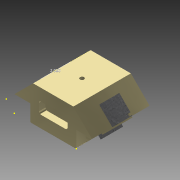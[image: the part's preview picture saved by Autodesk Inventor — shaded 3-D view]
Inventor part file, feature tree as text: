
AUTODESK INVENTOR PART (.ipt)
format: ipt  version: 2015 (Build 190159000, 159)  size: 1,916,928 bytes
history: native  units: in
note: dims shown in document units (in); Inventor stores cm internally (conversion verified against a paired STEP export)
features: sketch x15, extrude x10, plane x10, chamfer x4, mirror x3, fillet x2, other x1
ambient origin geometry x8: Origin, YZ Plane, XZ Plane, XY Plane, X Axis, Y Axis, Z Axis, Center Point
bodies: Solid1 (feature_tree)
feature tree (45):
  extrude  "Extrusion1"  Depth=3.06in
  chamfer  "Chamfer1"  Distance=5.0in
  chamfer  "Chamfer2"  Distance=1.625in Angle=45.0deg
  chamfer  "Chamfer3"  Distance=0.125in Angle=45.0deg
  chamfer  "Chamfer4"  Distance=1.625in Angle=45.0deg
  sketch  "Sketch2"  dims[d13=1.435in d14=0.125in d15=45.0deg d16=-1.38in]
  plane  "Work Plane1"
  plane  "Work Plane4"
  plane  "Work Plane5"
  plane  "Work Plane7"
  extrude  "Extrusion2"  [1 undecoded]
  extrude  "Extrusion3"  Depth=1.375in TaperAngle=0.0deg
  mirror  "Mirror1"
  extrude  "Extrusion4"  Depth=0.1in TaperAngle=0.0deg
  extrude  "Extrusion5"  Depth=0.3in TaperAngle=0.0deg
  extrude  "Extrusion6"  Depth=0.1in
  extrude  "Extrusion7"  Depth=1.0in
  sketch  "Sketch9"  dims[d36=1.03in d37=0.57in d38=0.0in d39=0.2in]
  plane  "Work Plane10"
  mirror  "Mirror2"
  mirror  "Mirror3"
  extrude  "Extrusion8"  Depth=0.745in
  sketch  "Sketch11"  dims[d43=0.795in]
  sketch  "Sketch12"  dims[d44=0.57in d45=0.0in]
  extrude  "Extrusion9"  Depth=0.57in TaperAngle=0.0deg
  fillet  "Fillet1"  Radius=0.2in
  extrude  "Extrusion10"  Depth=0.93in
  fillet  "Fillet2"  Radius=1.065in
  sketch  "Sketch15"
  sketch  "Sketch1"  dims[d0=6.75in d1=3.06in d2=5.0in d3=0.0in d4=1.625in d5=0.125in d6=45.0deg d7=1.435in d8=0.125in d9=45.0deg d10=1.625in d11=0.125in d12=45.0deg]
  plane  "Work Plane2"
  plane  "Work Plane3"
  plane  "Work Plane6"
  sketch  "Sketch3"  dims[d17=1.435in d18=1.375in d19=0.0in]
  sketch  "Sketch4"  dims[d20=1.375in d21=0.0in d22=0.1in d23=0.0in]
  sketch  "Sketch5"  dims[d24=0.1in d25=0.0in d26=0.3in d27=0.0in]
  sketch  "Sketch6"  dims[d28=0.1in d29=0.0in d30=0.36in]
  sketch  "Sketch7"  dims[d31=0.4in d32=0.0in d33=1.0in]
  sketch  "Sketch8"  dims[d34=2.5in d35=0.745in]
  plane  "Work Plane8"
  plane  "Work Plane9"
  sketch  "Sketch10"  dims[d40=2.4in d41=0.93in d42=1.065in]
  sketch  "Sketch13"  dims[d46=0.2in]
  sketch  "Sketch14"  dims[d48=2.0in]
  other  "Image1"
note: 1 required parameter value undecoded (feature->parameter linkage not recoverable at this tier; creation-order binding heuristic only, values carry confidence <= 0.55)
